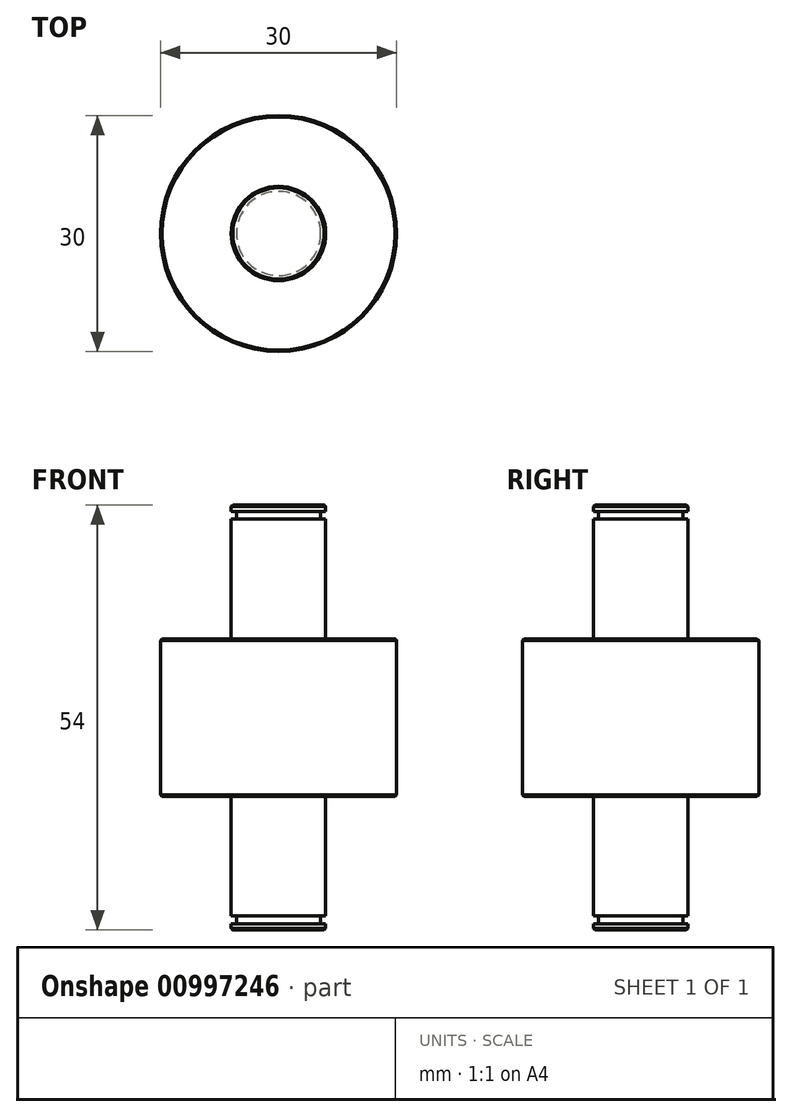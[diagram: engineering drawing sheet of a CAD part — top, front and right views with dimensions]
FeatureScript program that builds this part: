
annotation { "Feature Type Name" : "Feature", "Feature Type Description" : "" }
export const myFeature = defineFeature(function(context is Context, id is Id, definition is map)
    precondition{}
    {
        {
            var Q0;
            Q0=qCreatedBy(makeId("Front.planeOp"),FACE);
            var sketch = newSketch(context, id + "F0", { "sketchPlane" : qUnion([Q0])});
            skLineSegment(sketch, "E0", {"start": v(0, 27) * mm, "end": v(-6, 27) * mm});
            skLineSegment(sketch, "E1", {"start": v(-6, 27) * mm, "end": v(-6, 10) * mm});
            skLineSegment(sketch, "E2", {"start": v(-6, 10) * mm, "end": v(-15, 10) * mm});
            skLineSegment(sketch, "E3", {"start": v(-15, 10) * mm, "end": v(-15, -10) * mm});
            skLineSegment(sketch, "E4", {"start": v(-15, -10) * mm, "end": v(-6, -10) * mm});
            skLineSegment(sketch, "E5", {"start": v(-6, -10) * mm, "end": v(-6, -27) * mm});
            skLineSegment(sketch, "E6", {"start": v(-6, -27) * mm, "end": v(0, -27) * mm});
            skLineSegment(sketch, "E7", {"start": v(0, -27) * mm, "end": v(0, 27) * mm});
            skLineSegment(sketch, "E8", {"start": v(0, 58.87) * mm, "end": v(0, -50.94) * mm, "construction": true});
            skSolve(sketch);
        }
        {
            var Q0;
            Q0=makeQuery(id+"F0.imprint","IMPRINT",FACE,{"disambiguationData":[TD([[makeQuery(id+"F0.imprint","IMPRINT",EDGE,{"derivedFrom":sQuery(id+"F0.wireOp",EDGE,"E0")}),1.0]])]});
            var Q1;
            Q1=sQuery(id+"F0.wireOp",EDGE,"E8");
            revolve(context, id + "F1", {"surfaceOperationType" : NewSurfaceOperationType.NEW, "entities" : qUnion([Q0]), "axis" : qUnion([Q1]), "revolveType" : RevolveType.FULL});
        }
        {
            var Q0;
            Q0=makeQuery(id+"F1.opRevolve","SWEPT_EDGE",EDGE,{"disambiguationData":[OSD([sQuery(id+"F0.wireOp",EDGE,"E0"),sQuery(id+"F0.wireOp",EDGE,"E1")])]});
            var Q1;
            Q1=makeQuery(id+"F1.opRevolve","SWEPT_EDGE",EDGE,{"disambiguationData":[OSD([sQuery(id+"F0.wireOp",EDGE,"E2"),sQuery(id+"F0.wireOp",EDGE,"E3")])]});
            var Q2;
            Q2=makeQuery(id+"F1.opRevolve","SWEPT_EDGE",EDGE,{"disambiguationData":[OSD([sQuery(id+"F0.wireOp",EDGE,"E3"),sQuery(id+"F0.wireOp",EDGE,"E4")])]});
            var Q3;
            Q3=makeQuery(id+"F1.opRevolve","SWEPT_EDGE",EDGE,{"disambiguationData":[OSD([sQuery(id+"F0.wireOp",EDGE,"E5"),sQuery(id+"F0.wireOp",EDGE,"E6")])]});
            chamfer(context, id + "F2", {"entities" : qUnion([Q0, Q1, Q2, Q3]), "width" : 0.2 * mm, "tangentPropagation" : true});
        }
        {
            var Q0;
            Q0=qCreatedBy(makeId("Front.planeOp"),FACE);
            var sketch = newSketch(context, id + "F3", { "sketchPlane" : qUnion([Q0])});
            skLineSegment(sketch, "E9", {"start": v(-6, 26.2) * mm, "end": v(-5.35, 26.2) * mm});
            skLineSegment(sketch, "E10", {"start": v(-5.35, 26.2) * mm, "end": v(-5.35, 25.2) * mm});
            skLineSegment(sketch, "E11", {"start": v(-5.35, 25.2) * mm, "end": v(-6, 25.2) * mm});
            skLineSegment(sketch, "E12", {"start": v(-6, 26.2) * mm, "end": v(-6, 25.2) * mm});
            skLineSegment(sketch, "E13", {"start": v(0, 29.36) * mm, "end": v(0, -32.91) * mm, "construction": true});
            skLineSegment(sketch, "E14", {"start": v(-17.66, 0) * mm, "end": v(25.79, 0) * mm, "construction": true});
            skLineSegment(sketch, "E15.MirrorCS", {"start": v(-6, -26.2) * mm, "end": v(-5.35, -26.2) * mm});
            skLineSegment(sketch, "E16.MirrorCS", {"start": v(-5.35, -26.2) * mm, "end": v(-5.35, -25.2) * mm});
            skLineSegment(sketch, "E17.MirrorCS", {"start": v(-5.35, -25.2) * mm, "end": v(-6, -25.2) * mm});
            skLineSegment(sketch, "E18.MirrorCS", {"start": v(-6, -26.2) * mm, "end": v(-6, -25.2) * mm});
            skSolve(sketch);
        }
        {
            var Q0;
            Q0 = qSketchRegion(id + "F3", true);
            var Q1;
            Q1=sQuery(id+"F3.wireOp",EDGE,"E13");
            revolve(context, id + "F4", {"operationType" : NewBodyOperationType.REMOVE, "surfaceOperationType" : NewSurfaceOperationType.NEW, "entities" : qUnion([Q0]), "axis" : qUnion([Q1]), "revolveType" : RevolveType.FULL, "oppositeDirection" : true});
        }
        {
            var Q0;
            Q0=makeQuery(id+"F1.opRevolve","SWEPT_EDGE",EDGE,{"disambiguationData":[OSD([sQuery(id+"F0.wireOp",EDGE,"E1"),sQuery(id+"F0.wireOp",EDGE,"E2")])]});
            var Q1;
            Q1=makeQuery(id+"F1.opRevolve","SWEPT_EDGE",EDGE,{"disambiguationData":[OSD([sQuery(id+"F0.wireOp",EDGE,"E4"),sQuery(id+"F0.wireOp",EDGE,"E5")])]});
            fillet(context, id + "F5", {"entities" : qUnion([Q0, Q1]), "radius" : 0.2 * mm, "tangentPropagation" : true, "allowEdgeOverflow" : false});
        }
    });
